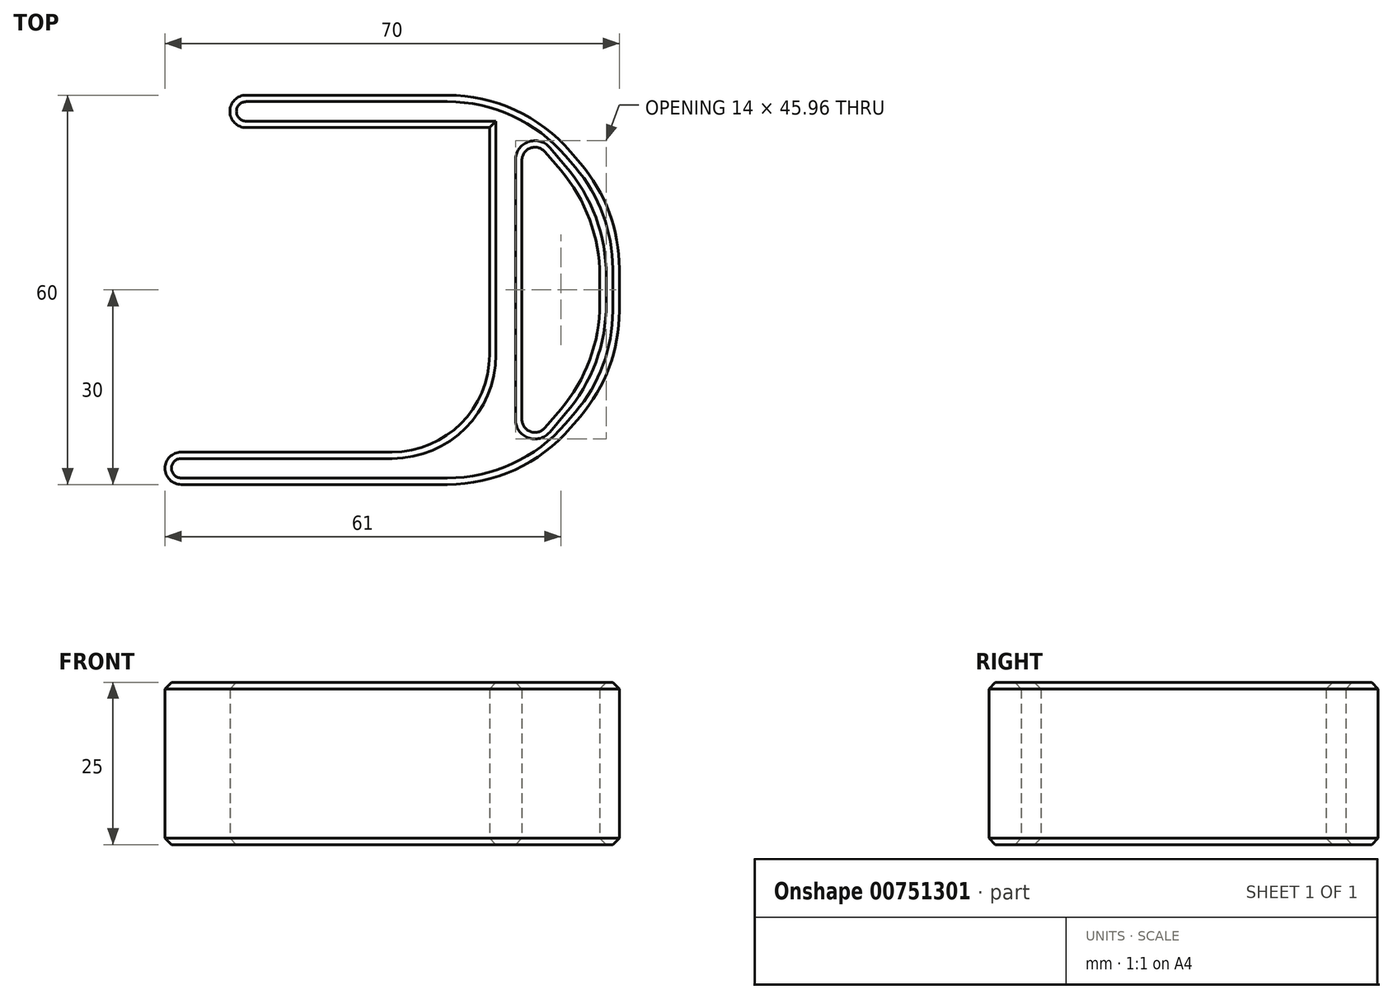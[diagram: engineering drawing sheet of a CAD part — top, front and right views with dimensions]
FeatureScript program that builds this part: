
annotation { "Feature Type Name" : "Feature", "Feature Type Description" : "" }
export const myFeature = defineFeature(function(context is Context, id is Id, definition is map)
    precondition{}
    {
        {
            var Q0;
            Q0=qCreatedBy(makeId("Top.planeOp"),FACE);
            var sketch = newSketch(context, id + "F0", { "sketchPlane" : qUnion([Q0])});
            skLineSegment(sketch, "E0", {"start": v(0, 0) * mm, "end": v(0, -50) * mm});
            skLineSegment(sketch, "E1", {"start": v(0, -50) * mm, "end": v(-50, -50) * mm});
            skLineSegment(sketch, "E2", {"start": v(0, 0) * mm, "end": v(-40, 0) * mm});
            skLineSegment(sketch, "E3.0", {"start": v(5, 5) * mm, "end": v(-40, 5) * mm});
            skLineSegment(sketch, "E3.1", {"start": v(5, 5) * mm, "end": v(5, -55) * mm});
            skLineSegment(sketch, "E3.2", {"start": v(5, -55) * mm, "end": v(-50, -55) * mm});
            skLineSegment(sketch, "E4", {"start": v(-40, 0) * mm, "end": v(-40, 5) * mm});
            skLineSegment(sketch, "E5", {"start": v(-50, -50) * mm, "end": v(-50, -55) * mm});
            skLineSegment(sketch, "E6", {"start": v(0, -25) * mm, "end": v(20, -25) * mm, "construction": true});
            skLineSegment(sketch, "E7", {"start": v(20, -37.5) * mm, "end": v(20, -12.5) * mm});
            skPoint(sketch, "E8", {"position": v(20, -25) * mm});
            skLineSegment(sketch, "E9", {"start": v(5, 5) * mm, "end": v(20, -12.5) * mm});
            skLineSegment(sketch, "E10", {"start": v(20, -37.5) * mm, "end": v(5, -55) * mm});
            skLineSegment(sketch, "E11", {"start": v(0, 0) * mm, "end": v(0, 5) * mm});
            skLineSegment(sketch, "E12.0", {"start": v(17, -36.4) * mm, "end": v(2.72, -53.05) * mm});
            skLineSegment(sketch, "E12.1", {"start": v(17, -36.4) * mm, "end": v(17, -13.6) * mm});
            skLineSegment(sketch, "E12.2", {"start": v(2.72, 3.05) * mm, "end": v(17, -13.6) * mm});
            skSolve(sketch);
        }
        {
            var Q0;
            Q0=makeQuery(id+"F0.imprint","IMPRINT",FACE,{"disambiguationData":[TD([[makeQuery(id+"F0.imprint","IMPRINT",EDGE,{"derivedFrom":sQuery(id+"F0.wireOp",EDGE,"E0")}),1.0]])]});
            var Q1;
            Q1=makeQuery(id+"F0.imprint","IMPRINT",FACE,{"disambiguationData":[TD([[makeQuery(id+"F0.imprint","IMPRINT",EDGE,{"derivedFrom":sQuery(id+"F0.wireOp",EDGE,"E3.1")}),1.0]])]});
            var Q2;
            Q2=makeQuery(id+"F0.imprint","IMPRINT",FACE,{"disambiguationData":[TD([[makeQuery(id+"F0.imprint","IMPRINT",EDGE,{"derivedFrom":sQuery(id+"F0.wireOp",EDGE,"E2")}),-1.0]])]});
            extrude(context, id + "F1", {"entities" : qUnion([Q0, Q1, Q2]), "depth" : 25 * mm, "offsetDistance" : 25 * mm});
        }
        {
            var Q0;
            Q0=makeQuery(id+"F1.opExtrude","SWEPT_EDGE",EDGE,{"disambiguationData":[OSD([sQuery(id+"F0.wireOp",EDGE,"E0"),sQuery(id+"F0.wireOp",EDGE,"E1")])]});
            fillet(context, id + "F2", {"entities" : qUnion([Q0]), "radius" : 15 * mm, "tangentPropagation" : true, "allowEdgeOverflow" : false});
        }
        {
            var Q0;
            Q0=makeQuery(id+"F1.opExtrude","SWEPT_EDGE",EDGE,{"disambiguationData":[OSD([sQuery(id+"F0.wireOp",EDGE,"E3.1"),sQuery(id+"F0.wireOp",EDGE,"E3.2"),sQuery(id+"F0.wireOp",EDGE,"E10")])]});
            var Q1;
            Q1=makeQuery(id+"F1.opExtrude","SWEPT_EDGE",EDGE,{"disambiguationData":[OSD([sQuery(id+"F0.wireOp",EDGE,"E7"),sQuery(id+"F0.wireOp",EDGE,"E10")])]});
            var Q2;
            Q2=makeQuery(id+"F1.opExtrude","SWEPT_EDGE",EDGE,{"disambiguationData":[OSD([sQuery(id+"F0.wireOp",EDGE,"E7"),sQuery(id+"F0.wireOp",EDGE,"E9")])]});
            var Q3;
            Q3=makeQuery(id+"F1.opExtrude","SWEPT_EDGE",EDGE,{"disambiguationData":[OSD([sQuery(id+"F0.wireOp",EDGE,"E3.0"),sQuery(id+"F0.wireOp",EDGE,"E3.1"),sQuery(id+"F0.wireOp",EDGE,"E9")])]});
            var Q4;
            Q4=makeQuery(id+"F1.opExtrude","SWEPT_EDGE",EDGE,{"disambiguationData":[OSD([sQuery(id+"F0.wireOp",EDGE,"E12.0"),sQuery(id+"F0.wireOp",EDGE,"E12.1")])]});
            var Q5;
            Q5=makeQuery(id+"F1.opExtrude","SWEPT_EDGE",EDGE,{"disambiguationData":[OSD([sQuery(id+"F0.wireOp",EDGE,"E12.1"),sQuery(id+"F0.wireOp",EDGE,"E12.2")])]});
            fillet(context, id + "F3", {"entities" : qUnion([Q0, Q1, Q2, Q3, Q4, Q5]), "radius" : 25 * mm, "tangentPropagation" : true, "allowEdgeOverflow" : false});
        }
        {
            var Q0;
            Q0=makeQuery(id+"F1.opExtrude","SWEPT_EDGE",EDGE,{"disambiguationData":[OSD([sQuery(id+"F0.wireOp",EDGE,"E3.2"),sQuery(id+"F0.wireOp",EDGE,"E5")])]});
            var Q1;
            Q1=makeQuery(id+"F1.opExtrude","SWEPT_EDGE",EDGE,{"disambiguationData":[OSD([sQuery(id+"F0.wireOp",EDGE,"E1"),sQuery(id+"F0.wireOp",EDGE,"E5")])]});
            var Q2;
            Q2=makeQuery(id+"F1.opExtrude","SWEPT_EDGE",EDGE,{"disambiguationData":[OSD([sQuery(id+"F0.wireOp",EDGE,"E2"),sQuery(id+"F0.wireOp",EDGE,"E4")])]});
            var Q3;
            Q3=makeQuery(id+"F1.opExtrude","SWEPT_EDGE",EDGE,{"disambiguationData":[OSD([sQuery(id+"F0.wireOp",EDGE,"E3.0"),sQuery(id+"F0.wireOp",EDGE,"E4")])]});
            fillet(context, id + "F4", {"entities" : qUnion([Q0, Q1, Q2, Q3]), "radius" : 2.5 * mm, "tangentPropagation" : true, "allowEdgeOverflow" : false});
        }
        {
            var Q0;
            Q0=makeQuery(id+"F1.opExtrude","SWEPT_EDGE",EDGE,{"disambiguationData":[OSD([sQuery(id+"F0.wireOp",EDGE,"E3.1"),sQuery(id+"F0.wireOp",EDGE,"E12.0")])]});
            var Q1;
            Q1=makeQuery(id+"F1.opExtrude","SWEPT_EDGE",EDGE,{"disambiguationData":[OSD([sQuery(id+"F0.wireOp",EDGE,"E3.1"),sQuery(id+"F0.wireOp",EDGE,"E12.2")])]});
            fillet(context, id + "F5", {"entities" : qUnion([Q0, Q1]), "radius" : 2 * mm, "tangentPropagation" : true, "allowEdgeOverflow" : false});
        }
        {
            var Q0;
            Q0=makeQuery(id+"F1.opExtrude","CAP_FACE",FACE,{"disambiguationData":[OSD([sQuery(id+"F0.wireOp",EDGE,"E0"),sQuery(id+"F0.wireOp",EDGE,"E1"),sQuery(id+"F0.wireOp",EDGE,"E2"),sQuery(id+"F0.wireOp",EDGE,"E3.0"),sQuery(id+"F0.wireOp",EDGE,"E3.2"),sQuery(id+"F0.wireOp",EDGE,"E4"),sQuery(id+"F0.wireOp",EDGE,"E5"),sQuery(id+"F0.wireOp",EDGE,"E7"),sQuery(id+"F0.wireOp",EDGE,"E9"),sQuery(id+"F0.wireOp",EDGE,"E10")])],"isStart":false});
            var Q1;
            Q1=makeQuery(id+"F1.opExtrude","CAP_FACE",FACE,{"disambiguationData":[OSD([sQuery(id+"F0.wireOp",EDGE,"E0"),sQuery(id+"F0.wireOp",EDGE,"E1"),sQuery(id+"F0.wireOp",EDGE,"E2"),sQuery(id+"F0.wireOp",EDGE,"E3.0"),sQuery(id+"F0.wireOp",EDGE,"E3.2"),sQuery(id+"F0.wireOp",EDGE,"E4"),sQuery(id+"F0.wireOp",EDGE,"E5"),sQuery(id+"F0.wireOp",EDGE,"E7"),sQuery(id+"F0.wireOp",EDGE,"E9"),sQuery(id+"F0.wireOp",EDGE,"E10")])],"isStart":true});
            chamfer(context, id + "F6", {"entities" : qUnion([Q0, Q1]), "width" : 1 * mm, "tangentPropagation" : true});
        }
    });
